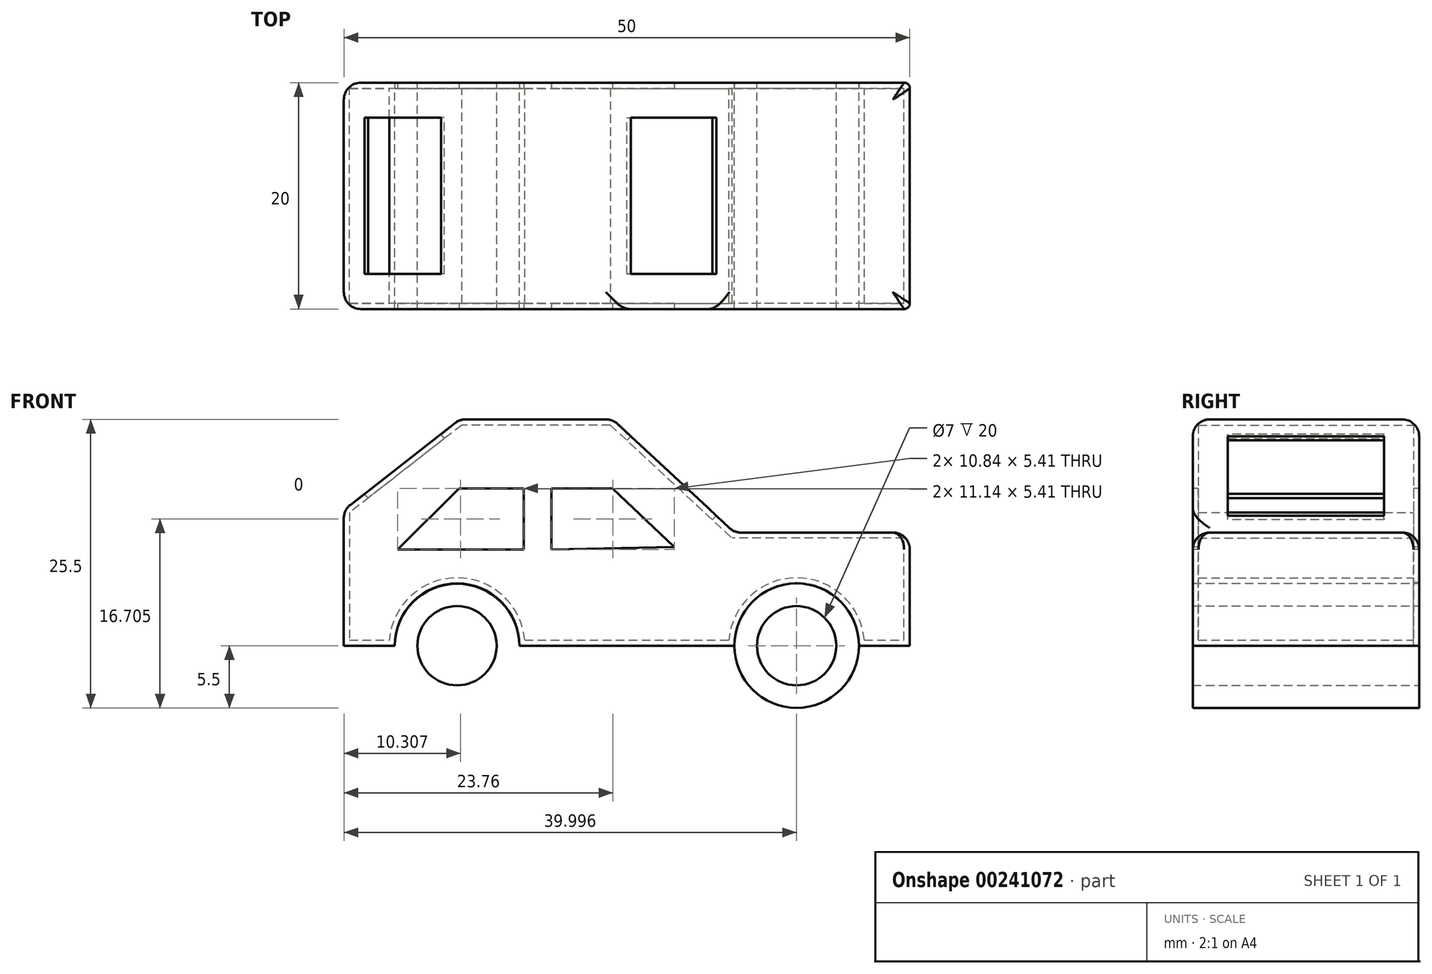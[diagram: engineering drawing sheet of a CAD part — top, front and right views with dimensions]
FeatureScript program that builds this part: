
annotation { "Feature Type Name" : "Feature", "Feature Type Description" : "" }
export const myFeature = defineFeature(function(context is Context, id is Id, definition is map)
    precondition{}
    {
        {
            var Q0;
            Q0=qCreatedBy(makeId("Front.planeOp"),FACE);
            var sketch = newSketch(context, id + "F0", { "sketchPlane" : qUnion([Q0])});
            skLineSegment(sketch, "E0", {"start": v(-23.74, 0) * mm, "end": v(26.26, 0) * mm});
            skLineSegment(sketch, "E1", {"start": v(26.26, 0) * mm, "end": v(26.26, 10) * mm});
            skLineSegment(sketch, "E2", {"start": v(26.26, 10) * mm, "end": v(10.76, 10) * mm});
            skLineSegment(sketch, "E3", {"start": v(10.76, 10) * mm, "end": v(10.76, 20) * mm});
            skLineSegment(sketch, "E4", {"start": v(10.76, 20) * mm, "end": v(-13.5, 20) * mm});
            skLineSegment(sketch, "E5", {"start": v(-13.5, 20) * mm, "end": v(-23.74, 12) * mm});
            skLineSegment(sketch, "E6", {"start": v(-23.74, 12) * mm, "end": v(-23.74, 0) * mm});
            skCircle(sketch, "E7", {"center": v(16.26, 0) * mm, "radius": 5.5 * mm});
            skCircle(sketch, "E8", {"center": v(16.26, 0) * mm, "radius": 3.5 * mm});
            skCircle(sketch, "E9", {"center": v(-13.74, 0) * mm, "radius": 5.5 * mm});
            skCircle(sketch, "E10", {"center": v(-13.74, 0) * mm, "radius": 3.5 * mm});
            skSolve(sketch);
        }
        {
            var Q0;
            {var subQ4=sQuery(id+"F0.wireOp",EDGE,"E1");Q0=makeQuery(id+"F0.imprint","IMPRINT",FACE,{"disambiguationData":[TD([[makeQuery(id+"F0.imprint","IMPRINT",EDGE,{"derivedFrom":subQ4}),1.0]])]});}
            extrude(context, id + "F1", {"entities" : qUnion([Q0]), "depth" : 10 * mm, "hasSecondDirection" : true, "secondDirectionOppositeDirection" : true, "secondDirectionDepth" : 9.5 * mm});
        }
        {
            var Q0;
            Q0=makeQuery(id+"F1.opExtrude","CAP_FACE",FACE,{"disambiguationData":[OSD([sQuery(id+"F0.wireOp",EDGE,"E0"),sQuery(id+"F0.wireOp",EDGE,"E1"),sQuery(id+"F0.wireOp",EDGE,"E2"),sQuery(id+"F0.wireOp",EDGE,"E3"),sQuery(id+"F0.wireOp",EDGE,"E4"),sQuery(id+"F0.wireOp",EDGE,"E5"),sQuery(id+"F0.wireOp",EDGE,"E6"),sQuery(id+"F0.wireOp",EDGE,"E7"),sQuery(id+"F0.wireOp",EDGE,"E9")])],"isStart":false});
            var sketch = newSketch(context, id + "F2", { "sketchPlane" : qUnion([Q0])});
            skLineSegment(sketch, "E11", {"start": v(10.76, 20) * mm, "end": v(10.76, 10) * mm});
            skLineSegment(sketch, "E12", {"start": v(10.76, 10) * mm, "end": v(10.76, 0) * mm});
            skLineSegment(sketch, "E13", {"start": v(10.76, 0) * mm, "end": v(0, 0) * mm});
            skLineSegment(sketch, "E14", {"start": v(0, 0) * mm, "end": v(0, 20) * mm});
            skLineSegment(sketch, "E15", {"start": v(0, 20) * mm, "end": v(10.76, 10) * mm});
            skSolve(sketch);
        }
        {
            var Q0;
            {var subQ0=sQuery(id+"F2.wireOp",EDGE,"E11");Q0=makeQuery(id+"F2.imprint","IMPRINT",FACE,{"disambiguationData":[TD([[makeQuery(id+"F2.imprint","IMPRINT",EDGE,{"derivedFrom":subQ0}),1.0]])]});}
            extrude(context, id + "F3", {"entities" : qUnion([Q0]), "operationType" : NewBodyOperationType.REMOVE, "endBound" : BoundingType.THROUGH_ALL, "oppositeDirection" : true, "depth" : 25 * mm});
        }
        {
            var Q0;
            Q0=makeQuery(id+"F1.opExtrude","CAP_FACE",FACE,{"disambiguationData":[OSD([sQuery(id+"F0.wireOp",EDGE,"E0"),sQuery(id+"F0.wireOp",EDGE,"E1"),sQuery(id+"F0.wireOp",EDGE,"E2"),sQuery(id+"F0.wireOp",EDGE,"E3"),sQuery(id+"F0.wireOp",EDGE,"E4"),sQuery(id+"F0.wireOp",EDGE,"E5"),sQuery(id+"F0.wireOp",EDGE,"E6"),sQuery(id+"F0.wireOp",EDGE,"E7"),sQuery(id+"F0.wireOp",EDGE,"E9")])],"isStart":true});
            shell(context, id + "F4", {"entities" : qUnion([Q0]), "thickness" : 0.5 * mm});
        }
        {
            var Q0;
            Q0=makeQuery(id+"F1.opExtrude","CAP_FACE",FACE,{"disambiguationData":[OSD([sQuery(id+"F0.wireOp",EDGE,"E0"),sQuery(id+"F0.wireOp",EDGE,"E1"),sQuery(id+"F0.wireOp",EDGE,"E2"),sQuery(id+"F0.wireOp",EDGE,"E3"),sQuery(id+"F0.wireOp",EDGE,"E4"),sQuery(id+"F0.wireOp",EDGE,"E5"),sQuery(id+"F0.wireOp",EDGE,"E6"),sQuery(id+"F0.wireOp",EDGE,"E7"),sQuery(id+"F0.wireOp",EDGE,"E9")])],"isStart":true});
            var sketch = newSketch(context, id + "F5", { "sketchPlane" : qUnion([Q0])});
            skLineSegment(sketch, "E16", {"start": v(-21.76, 0) * mm, "end": v(-26.26, 0) * mm});
            skLineSegment(sketch, "E17", {"start": v(-26.26, 0) * mm, "end": v(-26.26, 10) * mm});
            skLineSegment(sketch, "E18", {"start": v(-26.26, 10) * mm, "end": v(-10.76, 10) * mm});
            skLineSegment(sketch, "E19", {"start": v(-10.76, 10) * mm, "end": v(0, 20) * mm});
            skLineSegment(sketch, "E20", {"start": v(0, 20) * mm, "end": v(13.5, 20) * mm});
            skLineSegment(sketch, "E21", {"start": v(13.5, 20) * mm, "end": v(23.74, 12) * mm});
            skLineSegment(sketch, "E22", {"start": v(23.74, 12) * mm, "end": v(23.74, 0) * mm});
            skLineSegment(sketch, "E23", {"start": v(23.74, 0) * mm, "end": v(19.24, 0) * mm});
            skLineSegment(sketch, "E24", {"start": v(19.24, 0) * mm, "end": v(18.68, -0.25) * mm});
            skLineSegment(sketch, "E25", {"start": v(8.24, 0) * mm, "end": v(-10.76, 0) * mm});
            skArc(sketch, "E26", {"start": v(-10.76, 0) * mm, "mid": v(-16.26, 5.57) * mm, "end": v(-21.76, 0) * mm});
            skArc(sketch, "E27", {"start": v(19.24, 0) * mm, "mid": v(13.74, 5.47) * mm, "end": v(8.24, 0) * mm});
            skSolve(sketch);
        }
        {
            var Q0;
            Q0 = qSketchRegion(id + "F5", true);
            extrude(context, id + "F6", {"entities" : qUnion([Q0]), "operationType" : NewBodyOperationType.ADD, "depth" : 0.5 * mm});
        }
        {
            var Q0;
            Q0=makeQuery(id+"F6.boolean.opBoolean","MERGE",EDGE,{"derivedFrom":[makeQuery(id+"F1.opExtrude","SWEPT_EDGE",EDGE,{"disambiguationData":[OSD([sQuery(id+"F0.wireOp",EDGE,"E5"),sQuery(id+"F0.wireOp",EDGE,"E6")])]}),makeQuery(id+"F6.opExtrude","SWEPT_EDGE",EDGE,{"disambiguationData":[OSD([sQuery(id+"F5.wireOp",EDGE,"E21"),sQuery(id+"F5.wireOp",EDGE,"E22")])]})]});
            var Q1;
            Q1=makeQuery(id+"F1.opExtrude","CAP_EDGE",EDGE,{"disambiguationData":[OSD([sQuery(id+"F0.wireOp",EDGE,"E6")])],"isStart":false});
            var Q2;
            Q2=makeQuery(id+"F6.opExtrude","CAP_EDGE",EDGE,{"disambiguationData":[OSD([sQuery(id+"F5.wireOp",EDGE,"E22")])],"isStart":false});
            var Q3;
            Q3=makeQuery(id+"F1.opExtrude","CAP_EDGE",EDGE,{"disambiguationData":[OSD([sQuery(id+"F0.wireOp",EDGE,"E5")])],"isStart":false});
            var Q4;
            Q4=makeQuery(id+"F1.opExtrude","CAP_EDGE",EDGE,{"disambiguationData":[OSD([sQuery(id+"F0.wireOp",EDGE,"E4")])],"isStart":false});
            var Q5;
            Q5=makeQuery(id+"F3.boolean.opBoolean","COPY",EDGE,{"derivedFrom":makeQuery(id+"F3.opExtrude","CAP_EDGE",EDGE,{"disambiguationData":[OSD([sQuery(id+"F2.wireOp",EDGE,"E15")])],"isStart":true})});
            var Q6;
            Q6=makeQuery(id+"F1.opExtrude","CAP_EDGE",EDGE,{"disambiguationData":[OSD([sQuery(id+"F0.wireOp",EDGE,"E2")])],"isStart":false});
            var Q7;
            Q7=makeQuery(id+"F6.boolean.opBoolean","MERGE",EDGE,{"derivedFrom":[makeQuery(id+"F1.opExtrude","SWEPT_EDGE",EDGE,{"disambiguationData":[OSD([sQuery(id+"F0.wireOp",EDGE,"E1"),sQuery(id+"F0.wireOp",EDGE,"E2")])]}),makeQuery(id+"F6.opExtrude","SWEPT_EDGE",EDGE,{"disambiguationData":[OSD([sQuery(id+"F5.wireOp",EDGE,"E17"),sQuery(id+"F5.wireOp",EDGE,"E18")])]})]});
            var Q8;
            Q8=makeQuery(id+"F6.opExtrude","CAP_EDGE",EDGE,{"disambiguationData":[OSD([sQuery(id+"F5.wireOp",EDGE,"E18")])],"isStart":false});
            var Q9;
            Q9=makeQuery(id+"F6.opExtrude","CAP_EDGE",EDGE,{"disambiguationData":[OSD([sQuery(id+"F5.wireOp",EDGE,"E19")])],"isStart":false});
            var Q10;
            Q10=makeQuery(id+"F6.opExtrude","CAP_EDGE",EDGE,{"disambiguationData":[OSD([sQuery(id+"F5.wireOp",EDGE,"E20")])],"isStart":false});
            var Q11;
            Q11=makeQuery(id+"F6.opExtrude","CAP_EDGE",EDGE,{"disambiguationData":[OSD([sQuery(id+"F5.wireOp",EDGE,"E21")])],"isStart":false});
            var Q12;
            Q12=makeQuery(id+"F6.boolean.opBoolean","MERGE",EDGE,{"derivedFrom":[makeQuery(id+"F1.opExtrude","SWEPT_EDGE",EDGE,{"disambiguationData":[OSD([sQuery(id+"F0.wireOp",EDGE,"E4"),sQuery(id+"F0.wireOp",EDGE,"E5")])]}),makeQuery(id+"F6.opExtrude","SWEPT_EDGE",EDGE,{"disambiguationData":[OSD([sQuery(id+"F5.wireOp",EDGE,"E20"),sQuery(id+"F5.wireOp",EDGE,"E21")])]})]});
            var Q13;
            Q13=makeQuery(id+"F6.boolean.opBoolean","MERGE",EDGE,{"derivedFrom":[makeQuery(id+"F3.boolean.opBoolean","COPY",EDGE,{"derivedFrom":makeQuery(id+"F3.opExtrude","SWEPT_EDGE",EDGE,{"disambiguationData":[OSD([sQuery(id+"F0.wireOp",EDGE,"E4"),sQuery(id+"F2.wireOp",EDGE,"E14"),sQuery(id+"F2.wireOp",EDGE,"E15")])]})}),makeQuery(id+"F6.opExtrude","SWEPT_EDGE",EDGE,{"disambiguationData":[OSD([sQuery(id+"F5.wireOp",EDGE,"E19"),sQuery(id+"F5.wireOp",EDGE,"E20")])]})]});
            var Q14;
            {var subQ0=sQuery(id+"F0.wireOp",EDGE,"E2");Q14=makeQuery(id+"F6.boolean.opBoolean","MERGE",EDGE,{"derivedFrom":[makeQuery(id+"F3.boolean.opBoolean","MERGE",EDGE,{"derivedFrom":[makeQuery(id+"F1.opExtrude","SWEPT_EDGE",EDGE,{"disambiguationData":[OSD([subQ0,sQuery(id+"F0.wireOp",EDGE,"E3")])]}),makeQuery(id+"F3.opExtrude","SWEPT_EDGE",EDGE,{"disambiguationData":[OSD([subQ0,sQuery(id+"F2.wireOp",EDGE,"E11"),sQuery(id+"F2.wireOp",EDGE,"E12"),sQuery(id+"F2.wireOp",EDGE,"E15")])]})]}),makeQuery(id+"F6.opExtrude","SWEPT_EDGE",EDGE,{"disambiguationData":[OSD([sQuery(id+"F5.wireOp",EDGE,"E18"),sQuery(id+"F5.wireOp",EDGE,"E19")])]})]});}
            fillet(context, id + "F7", {"entities" : qUnion([Q0, Q1, Q2, Q3, Q4, Q5, Q6, Q7, Q8, Q9, Q10, Q11, Q12, Q13, Q14]), "radius" : 1.5 * mm, "tangentPropagation" : true, "allowEdgeOverflow" : false});
        }
        {
            var Q0;
            Q0=makeQuery(id+"F1.opExtrude","CAP_EDGE",EDGE,{"disambiguationData":[OSD([sQuery(id+"F0.wireOp",EDGE,"E1")])],"isStart":false});
            var Q1;
            Q1=makeQuery(id+"F6.opExtrude","CAP_EDGE",EDGE,{"disambiguationData":[OSD([sQuery(id+"F5.wireOp",EDGE,"E17")])],"isStart":false});
            fillet(context, id + "F8", {"entities" : qUnion([Q0, Q1]), "radius" : 0.5 * mm, "tangentPropagation" : true, "allowEdgeOverflow" : false});
        }
        {
            var Q0;
            Q0=makeQuery(id+"F1.opExtrude","CAP_FACE",FACE,{"disambiguationData":[OSD([sQuery(id+"F0.wireOp",EDGE,"E0"),sQuery(id+"F0.wireOp",EDGE,"E1"),sQuery(id+"F0.wireOp",EDGE,"E2"),sQuery(id+"F0.wireOp",EDGE,"E3"),sQuery(id+"F0.wireOp",EDGE,"E4"),sQuery(id+"F0.wireOp",EDGE,"E5"),sQuery(id+"F0.wireOp",EDGE,"E6"),sQuery(id+"F0.wireOp",EDGE,"E7"),sQuery(id+"F0.wireOp",EDGE,"E9")])],"isStart":false});
            var sketch = newSketch(context, id + "F9", { "sketchPlane" : qUnion([Q0])});
            skLineSegment(sketch, "E28", {"start": v(5.44, 8.7) * mm, "end": v(0, 13.91) * mm});
            skPoint(sketch, "E28.startSnap0", {"position": v(10.25, 8.7) * mm});
            skLineSegment(sketch, "E29", {"start": v(0, 13.91) * mm, "end": v(-5.4, 13.91) * mm});
            skLineSegment(sketch, "E30", {"start": v(-5.4, 13.91) * mm, "end": v(-5.4, 8.5) * mm});
            skLineSegment(sketch, "E31", {"start": v(-5.4, 8.5) * mm, "end": v(5.44, 8.7) * mm});
            skLineSegment(sketch, "E32", {"start": v(-7.86, 8.5) * mm, "end": v(-19, 8.5) * mm});
            skLineSegment(sketch, "E33", {"start": v(-19, 8.5) * mm, "end": v(-13.58, 13.91) * mm});
            skLineSegment(sketch, "E34", {"start": v(-13.58, 13.91) * mm, "end": v(-7.86, 13.91) * mm});
            skLineSegment(sketch, "E35", {"start": v(-7.86, 13.91) * mm, "end": v(-7.86, 8.5) * mm});
            skSolve(sketch);
        }
        {
            var Q0;
            Q0 = qSketchRegion(id + "F9", true);
            extrude(context, id + "F10", {"entities" : qUnion([Q0]), "operationType" : NewBodyOperationType.REMOVE, "oppositeDirection" : true, "depth" : 25 * mm});
        }
        {
            var Q0;
            Q0=makeQuery(id+"F6.boolean.opBoolean","MERGE",FACE,{"derivedFrom":[makeQuery(id+"F3.boolean.opBoolean","COPY",FACE,{"derivedFrom":makeQuery(id+"F3.opExtrude","SWEPT_FACE",FACE,{"disambiguationData":[OSD([sQuery(id+"F2.wireOp",EDGE,"E15")])]})}),makeQuery(id+"F6.opExtrude","SWEPT_FACE",FACE,{"disambiguationData":[OSD([sQuery(id+"F5.wireOp",EDGE,"E19")])]})]});
            var sketch = newSketch(context, id + "F11", { "sketchPlane" : qUnion([Q0])});
            skLineSegment(sketch, "E36", {"start": v(-11.43, -6.9) * mm, "end": v(-1.12, -6.9) * mm});
            skLineSegment(sketch, "E37", {"start": v(-1.12, -6.9) * mm, "end": v(-1.12, 6.9) * mm});
            skLineSegment(sketch, "E38", {"start": v(-1.12, 6.9) * mm, "end": v(-11.43, 6.9) * mm});
            skLineSegment(sketch, "E39", {"start": v(-11.43, 6.9) * mm, "end": v(-11.43, -6.9) * mm});
            skSolve(sketch);
        }
        {
            var Q0;
            Q0 = qSketchRegion(id + "F11", true);
            extrude(context, id + "F12", {"entities" : qUnion([Q0]), "operationType" : NewBodyOperationType.REMOVE, "oppositeDirection" : true, "depth" : 5 * mm});
        }
        {
            var Q0;
            Q0=makeQuery(id+"F6.boolean.opBoolean","MERGE",FACE,{"derivedFrom":[makeQuery(id+"F1.opExtrude","SWEPT_FACE",FACE,{"disambiguationData":[OSD([sQuery(id+"F0.wireOp",EDGE,"E5")])]}),makeQuery(id+"F6.opExtrude","SWEPT_FACE",FACE,{"disambiguationData":[OSD([sQuery(id+"F5.wireOp",EDGE,"E21")])]})]});
            var sketch = newSketch(context, id + "F13", { "sketchPlane" : qUnion([Q0])});
            skLineSegment(sketch, "E40", {"start": v(-9, 6.9) * mm, "end": v(-0.45, 6.9) * mm});
            skLineSegment(sketch, "E41", {"start": v(-0.45, 6.9) * mm, "end": v(-0.45, -6.9) * mm});
            skLineSegment(sketch, "E42", {"start": v(-0.45, -6.9) * mm, "end": v(-9, -6.9) * mm});
            skLineSegment(sketch, "E43", {"start": v(-9, -6.9) * mm, "end": v(-9, 6.9) * mm});
            skSolve(sketch);
        }
        {
            var Q0;
            Q0 = qSketchRegion(id + "F13", true);
            extrude(context, id + "F14", {"entities" : qUnion([Q0]), "operationType" : NewBodyOperationType.REMOVE, "oppositeDirection" : true, "depth" : 5 * mm});
        }
        {
            var Q0;
            {var subQ0=sQuery(id+"F0.wireOp",EDGE,"E8");var subQ1=sQuery(id+"F0.wireOp",EDGE,"E0");var subQ2=makeQuery(id+"F0.imprint","INTERSECT",VERTEX,{"disambiguationData":[OD(0.0)],"derivedFrom":[subQ1,subQ0]});Q0=makeQuery(id+"F0.imprint","IMPRINT",FACE,{"disambiguationData":[TD([[makeQuery(id+"F0.imprint","IMPRINT",EDGE,{"disambiguationData":[TD([[subQ2,-1.0]])],"derivedFrom":subQ1}),-1.0]])]});}
            var Q1;
            {var subQ0=sQuery(id+"F0.wireOp",EDGE,"E8");var subQ1=sQuery(id+"F0.wireOp",EDGE,"E0");var subQ2=makeQuery(id+"F0.imprint","INTERSECT",VERTEX,{"disambiguationData":[OD(0.0)],"derivedFrom":[subQ1,subQ0]});Q1=makeQuery(id+"F0.imprint","IMPRINT",FACE,{"disambiguationData":[TD([[makeQuery(id+"F0.imprint","IMPRINT",EDGE,{"disambiguationData":[TD([[subQ2,-1.0]])],"derivedFrom":subQ1}),1.0]])]});}
            var Q2;
            {var subQ0=sQuery(id+"F0.wireOp",EDGE,"E10");var subQ1=sQuery(id+"F0.wireOp",EDGE,"E0");var subQ2=makeQuery(id+"F0.imprint","INTERSECT",VERTEX,{"disambiguationData":[OD(0.0)],"derivedFrom":[subQ1,subQ0]});Q2=makeQuery(id+"F0.imprint","IMPRINT",FACE,{"disambiguationData":[TD([[makeQuery(id+"F0.imprint","IMPRINT",EDGE,{"disambiguationData":[TD([[subQ2,-1.0]])],"derivedFrom":subQ1}),-1.0]])]});}
            var Q3;
            {var subQ0=sQuery(id+"F0.wireOp",EDGE,"E10");var subQ1=sQuery(id+"F0.wireOp",EDGE,"E0");var subQ2=makeQuery(id+"F0.imprint","INTERSECT",VERTEX,{"disambiguationData":[OD(0.0)],"derivedFrom":[subQ1,subQ0]});Q3=makeQuery(id+"F0.imprint","IMPRINT",FACE,{"disambiguationData":[TD([[makeQuery(id+"F0.imprint","IMPRINT",EDGE,{"disambiguationData":[TD([[subQ2,-1.0]])],"derivedFrom":subQ1}),1.0]])]});}
            extrude(context, id + "F15", {"entities" : qUnion([Q0, Q1, Q2, Q3]), "endBound" : BoundingType.SYMMETRIC, "depth" : 20 * mm});
        }
    });
